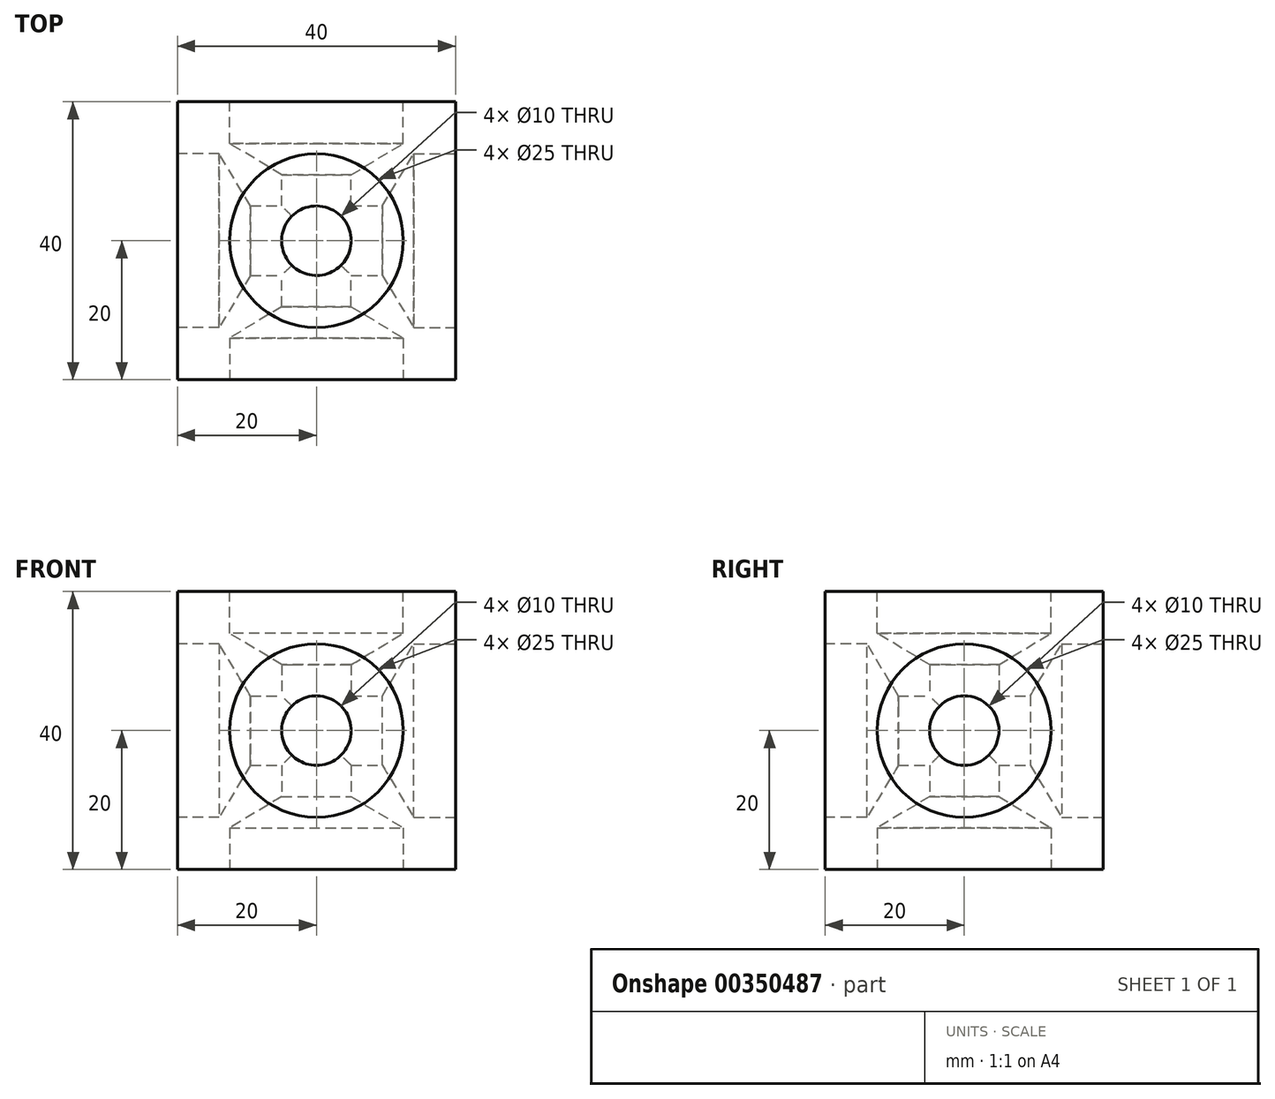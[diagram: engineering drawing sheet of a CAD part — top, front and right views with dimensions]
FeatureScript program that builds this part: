
annotation { "Feature Type Name" : "Feature", "Feature Type Description" : "" }
export const myFeature = defineFeature(function(context is Context, id is Id, definition is map)
    precondition{}
    {
        {
            var Q0;
            Q0=qCreatedBy(makeId("Top.planeOp"),FACE);
            var sketch = newSketch(context, id + "F0", { "sketchPlane" : qUnion([Q0])});
            skLineSegment(sketch, "E0.bottom", {"start": v(20, -20) * mm, "end": v(-20, -20) * mm});
            skLineSegment(sketch, "E0.top", {"start": v(20, 20) * mm, "end": v(-20, 20) * mm});
            skLineSegment(sketch, "E0.left", {"start": v(20, -20) * mm, "end": v(20, 20) * mm});
            skLineSegment(sketch, "E0.right", {"start": v(-20, -20) * mm, "end": v(-20, 20) * mm});
            skPoint(sketch, "E0.middle", {"position": v(0, 0) * mm});
            skSolve(sketch);
        }
        {
            var Q0;
            Q0 = qSketchRegion(id + "F0", true);
            extrude(context, id + "F1", {"entities" : qUnion([Q0]), "endBound" : BoundingType.SYMMETRIC, "depth" : 40 * mm});
        }
        {
            var Q0;
            Q0=makeQuery(id+"F1.opExtrude","SWEPT_FACE",FACE,{"disambiguationData":[OSD([sQuery(id+"F0.wireOp",EDGE,"E0.left")])]});
            var sketch = newSketch(context, id + "F2", { "sketchPlane" : qUnion([Q0])});
            skPoint(sketch, "E1", {"position": v(0, 0) * mm});
            skPoint(sketch, "E2", {"position": v(-10.03, 9.85) * mm});
            skSolve(sketch);
        }
        {
            var Q0;
            Q0=makeQuery(id+"F1.opExtrude","SWEPT_FACE",FACE,{"disambiguationData":[OSD([sQuery(id+"F0.wireOp",EDGE,"E0.top")])]});
            var sketch = newSketch(context, id + "F3", { "sketchPlane" : qUnion([Q0])});
            skPoint(sketch, "E3", {"position": v(0, 0) * mm});
            skSolve(sketch);
        }
        {
            var Q0;
            Q0=makeQuery(id+"F1.opExtrude","CAP_FACE",FACE,{"disambiguationData":[OSD([sQuery(id+"F0.wireOp",EDGE,"E0.bottom"),sQuery(id+"F0.wireOp",EDGE,"E0.top"),sQuery(id+"F0.wireOp",EDGE,"E0.left"),sQuery(id+"F0.wireOp",EDGE,"E0.right")])],"isStart":true});
            var sketch = newSketch(context, id + "F4", { "sketchPlane" : qUnion([Q0])});
            skPoint(sketch, "E4", {"position": v(0, 0) * mm});
            skSolve(sketch);
        }
        {
            var Q0;
            Q0=makeQuery(id+"F1.opExtrude","CAP_FACE",FACE,{"disambiguationData":[OSD([sQuery(id+"F0.wireOp",EDGE,"E0.bottom"),sQuery(id+"F0.wireOp",EDGE,"E0.top"),sQuery(id+"F0.wireOp",EDGE,"E0.left"),sQuery(id+"F0.wireOp",EDGE,"E0.right")])],"isStart":false});
            var sketch = newSketch(context, id + "F5", { "sketchPlane" : qUnion([Q0])});
            skPoint(sketch, "E5", {"position": v(0, 0) * mm});
            skSolve(sketch);
        }
        {
            var Q0;
            Q0=makeQuery(id+"F1.opExtrude","SWEPT_FACE",FACE,{"disambiguationData":[OSD([sQuery(id+"F0.wireOp",EDGE,"E0.right")])]});
            var sketch = newSketch(context, id + "F6", { "sketchPlane" : qUnion([Q0])});
            skPoint(sketch, "E6", {"position": v(0, 0) * mm});
            skSolve(sketch);
        }
        {
            var Q0;
            Q0=makeQuery(id+"F1.opExtrude","SWEPT_FACE",FACE,{"disambiguationData":[OSD([sQuery(id+"F0.wireOp",EDGE,"E0.bottom")])]});
            var sketch = newSketch(context, id + "F7", { "sketchPlane" : qUnion([Q0])});
            skPoint(sketch, "E7", {"position": v(0, 0) * mm});
            skSolve(sketch);
        }
        {
            var Q0;
            Q0=sQuery(id+"F4.wireOp",VERTEX,"E4");
            var Q1;
            Q1=sQuery(id+"F3.wireOp",VERTEX,"E3");
            var Q2;
            Q2=sQuery(id+"F2.wireOp",VERTEX,"E1");
            var Q3;
            Q3=makeQuery(id+"F1.opExtrude","SWEPT_BODY",BODY,{"disambiguationData":[OSD([sQuery(id+"F0.wireOp",EDGE,"E0.bottom"),sQuery(id+"F0.wireOp",EDGE,"E0.top"),sQuery(id+"F0.wireOp",EDGE,"E0.left"),sQuery(id+"F0.wireOp",EDGE,"E0.right")])]});
            hole(context, id + "F8", {"style" : HoleStyle.SIMPLE, "endStyle" : HoleEndStyle.THROUGH, "holeDiameter" : 10 * mm, "isTappedThrough" : true, "tappedDepth" : 12 * mm, "tapClearance" : 3, "locations" : qUnion([Q0, Q1, Q2]), "scope" : qUnion([Q3])});
        }
        {
            var Q0;
            Q0=sQuery(id+"F4.wireOp",VERTEX,"E4");
            var Q1;
            Q1=sQuery(id+"F3.wireOp",VERTEX,"E3");
            var Q2;
            Q2=sQuery(id+"F2.wireOp",VERTEX,"E1");
            var Q3;
            Q3=sQuery(id+"F7.wireOp",VERTEX,"E7");
            var Q4;
            Q4=sQuery(id+"F6.wireOp",VERTEX,"E6");
            var Q5;
            Q5=sQuery(id+"F5.wireOp",VERTEX,"E5");
            var Q6;
            Q6=makeQuery(id+"F1.opExtrude","SWEPT_BODY",BODY,{"disambiguationData":[OSD([sQuery(id+"F0.wireOp",EDGE,"E0.bottom"),sQuery(id+"F0.wireOp",EDGE,"E0.top"),sQuery(id+"F0.wireOp",EDGE,"E0.left"),sQuery(id+"F0.wireOp",EDGE,"E0.right")])]});
            hole(context, id + "F9", {"style" : HoleStyle.SIMPLE, "endStyle" : HoleEndStyle.BLIND, "holeDiameter" : 25 * mm, "holeDepth" : 6 * mm, "isTappedThrough" : true, "tappedDepth" : 12 * mm, "tapClearance" : 3, "locations" : qUnion([Q0, Q1, Q2, Q3, Q4, Q5]), "scope" : qUnion([Q6])});
        }
        {
            var Q0;
            Q0=makeQuery(id+"F1.opExtrude","SWEPT_BODY",BODY,{"disambiguationData":[OSD([sQuery(id+"F0.wireOp",EDGE,"E0.bottom"),sQuery(id+"F0.wireOp",EDGE,"E0.top"),sQuery(id+"F0.wireOp",EDGE,"E0.left"),sQuery(id+"F0.wireOp",EDGE,"E0.right")])]});
            transform(context, id + "F10", {"entities" : qUnion([Q0]), "transformType" : TransformType.TRANSLATION_3D, "dx" : 0 * mm, "dy" : 0 * mm, "dz" : 0 * mm, "makeCopy" : true});
        }
    });
